# Revit family: ON5DMHX-NRG
name_source: partatom
category: Mechanical Equipment
units: mm (PartAtom-declared; Revit-internal decimal feet)

## family parameters
Always vertical = Yes
Cut with Voids When Loaded = No
OmniClass Number = 23.40.40.11.17
OmniClass Title = Refrigerated Cases
Part Type = Normal
Room Calculation Point = No
Round Connector Dimension = Use Radius
Shared = No
Work Plane-Based = Yes

## types (13) — shared parameters
16" Shelf = Yes
18" Shelf = Yes
BOTTOM ELECTRICAL = Yes
BOTTOM REFRIGERATION PIPING = Yes
Certifications = NSF 7, UL471, CSA
DATE = 03/14/2017
DRAIN LINE = 48"
DRAIN PIPING = Yes
Default Elevation = 48"
Description = Narrow Self-Contained Multi-Deck Merchandiser
Discharge Air Velocity (FPM) = 210 FPM
Drain Pump Amps = 0 A
Drain Pump Watts = 0 W
EQUIPMENT DESCRIPTION = Narrow Self-Contained Multi-Deck Merchandiser
EQUIPMENT MARK = ON5DMHX-NRG
Evaporator Pan Heater  Amps = 0 A
Evaporator Pan Heater  Watts = 0 W
Frequency (Hz) = 0 Hz
GLASS = Glass
Height = 84 7/8"
High Efficiency Fan Amps = 0 A
High Efficiency Fan Watts = 0 W
High Power (Cornice) Amps = 0 A
Horsepower = 0
Item Description = Narrow Self-Contained Multi-Deck Merchandiser
LF STD END = Yes
Lbs. Of Refrigerant = 0
Legend Number = ON5DMHX-NRG
Locked Rotor Amps (LRA) (Amps) = 0 A
Manufacturer = HILL PHOENIX
Maximum Lights Amps = 0 A
Maximum Lights Watts = 0 W
Maximum Overcurrent Protection = 0 A
Minimum Circuit Ampacity = 0 A
Model = ON5DMHX-NRG
PAINTED METAL UPPER SHELF = PAINTED SHELVES
REAR REFRIGERATION PIPING = Yes
REF = 28 5/8"
REFRIGERATION PIPING = COPPER PIPE
RT STD END = Yes
Refgn = 8 3/4"
Refrigerant = 0
Running Load Amps (RLA) (Amps) = 0 A
STAINLESS STEEL = GALVANIZED STEEL
Standard Power Amps = 0 A
Suction Pressure @ Case Outlet (psig) = 0
Superheat Set Point @ Bulb (°F) = 6-8 °F
TOP ELECTRICAL = Yes
TOP REFRIGERATION PIPING = Yes
Timed-Off Defrost Fail-Safe (Min) = - (Min)
Timed-Off Defrost Termination Temp = 42 °F
URL = http://www.hillphoenix.com
Volts = 0 V
Width = 35 3/4"
Wire = 0
zero-valued in all types: Number of Fans, PHASE

## per-type parameters (varying)
| type | BTUH Conventional | BTUH Parallel | CENTER LINE | Defrosts Per Day | Discharge Air (°F) | Evaporator (°F) | High Efficiency Amps | High Efficiency Watts | High Power (Cornice) Watts | Length | Length of Cases | Light Length | Lights Per Row | Standard Power Watts | TIMED OFF DEFROST FAIL-SAFE (Min) |
| 08' | 1611 | 1410 | 48" | 6 | 31 °F | 28 °F | 0 A | 35 W | 24 W | 96" | 96" | 3' | 2 | 9 W | 40 |
| 06' | 1651 | 1445 | 36" | 2 | 31 °F | 28 °F | 0 A | 18 W | 15 W | 72" | 72" | 4' | 1 | 6 W | 30 |
| Sample 1 (4') | 1583 | 1385 | 48" | 0 | 31 °F | 28 °F | 0 A | 35 W | 30 W | 96" | 96" | 4' | 2 | 12 W |  |
| Sample 2 (12') | 1560 | 1365 | 48" | 0 | 31 °F | 28 °F | 1 A | 53 W | 45 W | 96" | 96" | 4' | 3 | 18 W |  |
| Std. Dairy | 1270 | 1235 | 48" | 2 | 37 °F | 34 °F | 0 A | 35 W | 30 W | 96" | 96" | 3' | 2 | 17 W | 30 |
| 2.5" Ext | 1231 | 1200 | 48" | 2 | 37 °F | 34 °F | 0 A | 35 W | 30 W | 96" | 96" | 3' | 2 | 17 W |  |
| 5" Ext | 1209 | 1175 | 48" | 2 | 37 °F | 34 °F | 0 A | 35 W | 30 W | 96" | 96" | 3' | 2 | 17 W |  |
| 7.5" Ext | 1188 | 1155 | 48" | 2 | 37 °F | 34 °F | 0 A | 35 W | 30 W | 96" | 96" | 3' | 2 | 17 W | 40 |
| 04' | 1651 | 1445 | 24" | 6 | 33 °F | 28 °F | 0 A | 18 W | 15 W | 48" | 72" | 4' | 1 | 6 W | 40 |
| 09' | 1611 | 1410 | 54" | 2 | 33 °F | 28 °F | 0 A | 35 W | 24 W | 108" | 96" | 3' | 2 | 9 W | 30 |
| 10' | 1611 | 1410 | 60" | 2 | 33 °F | 28 °F | 0 A | 35 W | 24 W | 120" | 96" | 3' | 2 | 9 W | 30 |
| 12' | 1611 | 1410 | 72" | 2 | 33 °F | 28 °F | 0 A | 35 W | 24 W | 144" | 96" | 3' | 2 | 9 W | 30 |
| 12s3 | 1611 | 1410 | 72" | 2 | 33 °F | 28 °F | 0 A | 35 W | 24 W | 144" | 96" | 3' | 2 | 9 W | 30 |

## geometry (parser evidence)
native form markers: Blend x17, Sweep x7
no freeform markers — native parametric forms only
